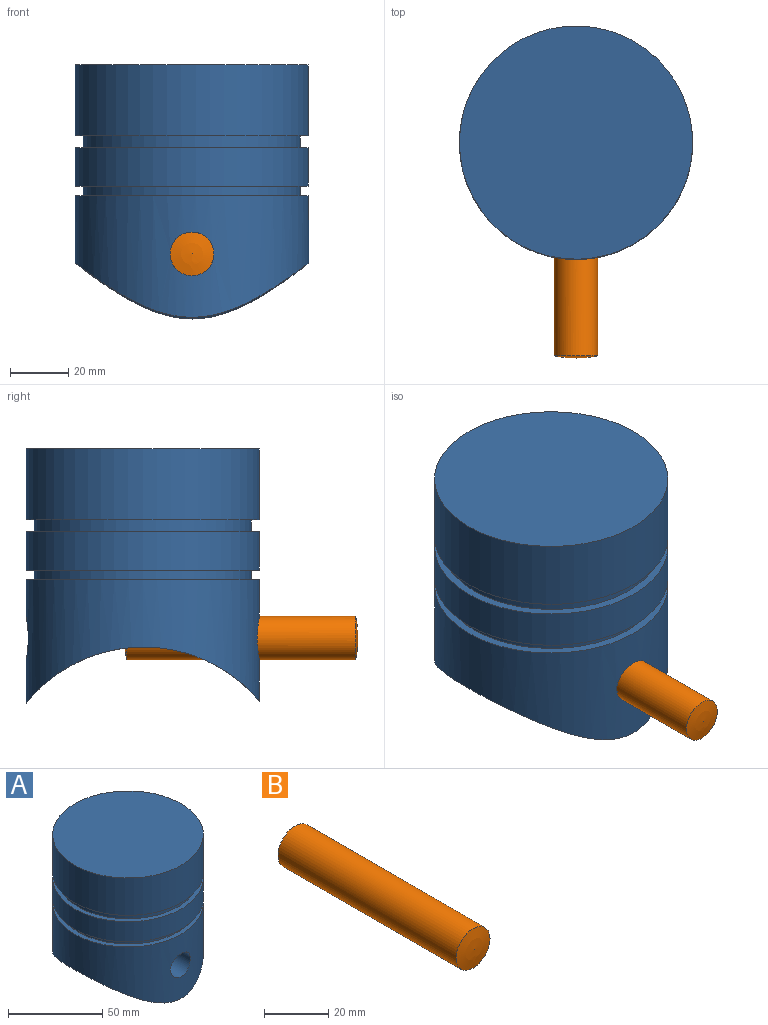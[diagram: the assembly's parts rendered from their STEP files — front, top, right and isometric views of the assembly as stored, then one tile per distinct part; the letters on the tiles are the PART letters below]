
ASSEMBLY  parts=2 mates=1
PART A: 15 faces, bbox 80x80x87.1 mm
  f0: cylinder r=28.53mm len=61.77mm, axis (0,0,-1), area 9902.2mm2, adj f3,f12,f13,f14
  f1: cylinder r=40mm len=80mm, axis (0,0,-1), area 7699.3mm2, adj f4,f12,f13,f14
  f2: plane 80x80mm, normal (0,0,1), area 5026.5mm2, adj f11
  f3: plane 57.07x57.07mm, normal (0,0,-1), area 2557.6mm2, adj f0
  f4: plane 80x80mm, normal (0,0,1), area 662.8mm2, adj f1,f5
  f5: cylinder r=37.27mm len=74.54mm, axis (0,0,-1), area 767.3mm2, adj f4,f6
  f6: plane 80x80mm, normal (0,0,-1), area 662.8mm2, adj f5,f7
  f7: cylinder r=40mm len=80mm, axis (0,0,-1), area 3293.8mm2, adj f6,f8
  f8: plane 80x80mm, normal (0,0,1), area 662.8mm2, adj f7,f9
  f9: cylinder r=37.27mm len=74.54mm, axis (0,0,-1), area 959.1mm2, adj f8,f10
  f10: plane 80x80mm, normal (0,0,-1), area 662.8mm2, adj f9,f11
  f11: cylinder r=40mm len=80mm, axis (0,0,-1), area 6107.3mm2, adj f2,f10
  f12: cylinder r=7.5mm len=15mm, axis (0,-1,0), area 547.3mm2, adj f0,f1
  f13: cylinder r=7.5mm len=15mm, axis (0,-1,0), area 547.2mm2, adj f0,f1
  f14: cylinder r=51.81mm len=80mm, axis (-1,0,0), area 2861.5mm2, adj f0,f1
PART B: 3 faces, bbox 15x80x15 mm
  f0: sphere r=40mm, area 178.3mm2, adj f1
  f1: cylinder r=7.5mm len=78.58mm, axis (0,1,0), area 3703.1mm2, adj f0,f2
  f2: sphere r=40mm, area 178.3mm2, adj f1
PLACE A t=(-0.15,0.27,0.53)mm
PLACE B t=(-0.15,-33.5,-49.37)mm
MATE slider B.f1 <-> A.f12  axis (0,1,0) through (-0.15,-33.5,-49.37)mm
